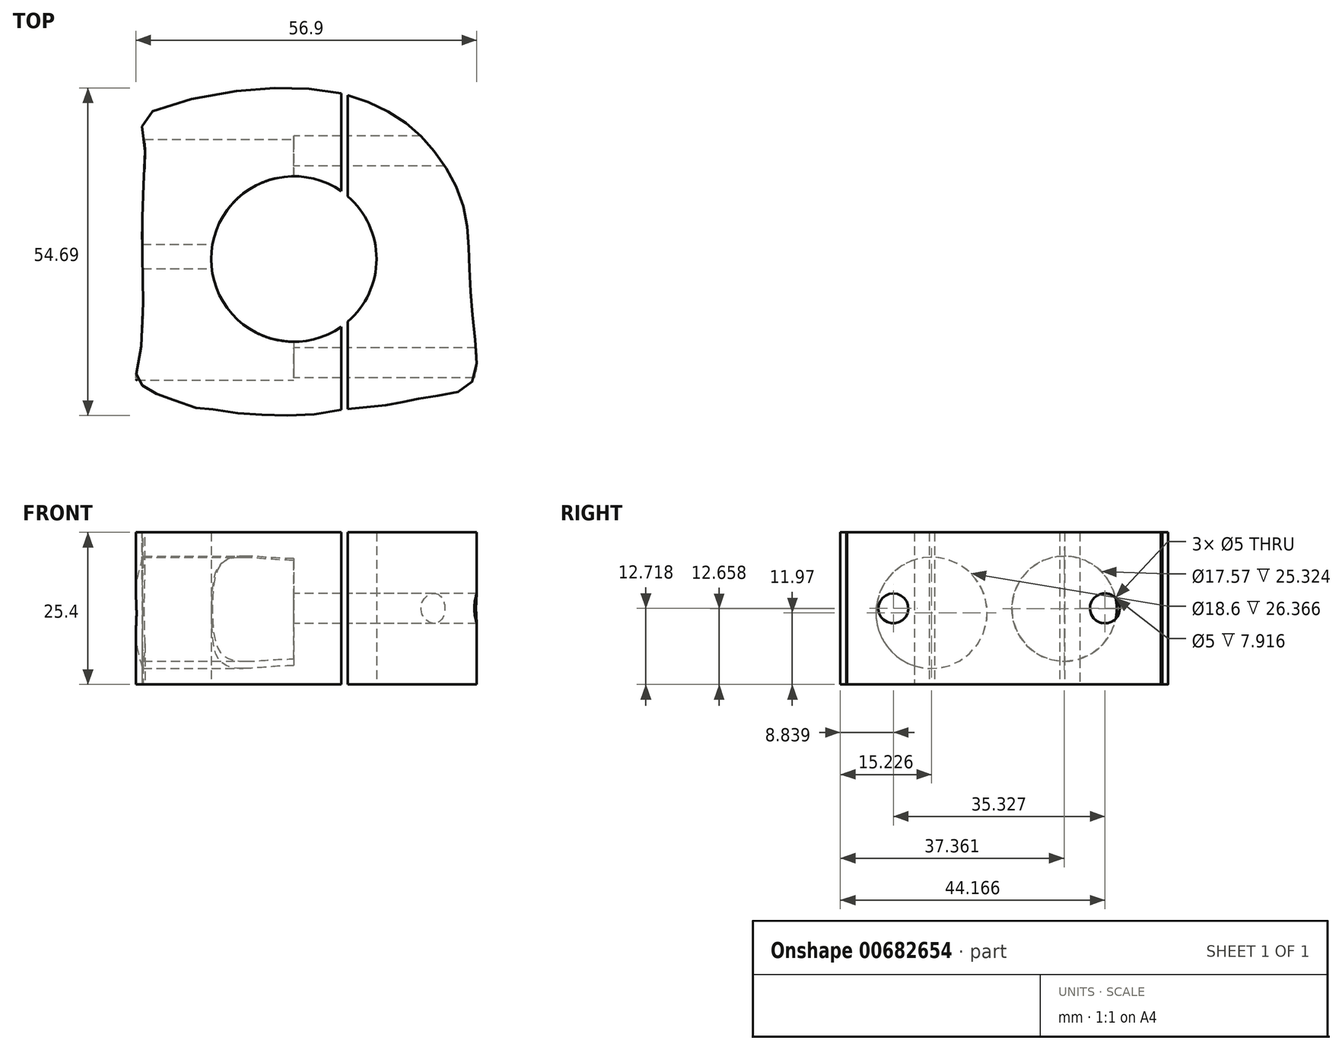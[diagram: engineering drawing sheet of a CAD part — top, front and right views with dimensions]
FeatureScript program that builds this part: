
annotation { "Feature Type Name" : "Feature", "Feature Type Description" : "" }
export const myFeature = defineFeature(function(context is Context, id is Id, definition is map)
    precondition{}
    {
        {
            var Q0;
            Q0=qCreatedBy(makeId("Top.planeOp"),FACE);
            var sketch = newSketch(context, id + "F0", { "sketchPlane" : qUnion([Q0])});
            skCircle(sketch, "E0", {"center": v(0, 0) * mm, "radius": 13.8 * mm});
            skFitSpline(sketch, "E1", {"points": [v(-26.3, -20.13) * mm, v(-25.31, -21.11) * mm, v(-23.34, -22.35) * mm, v(-20.62, -23.34) * mm, v(-16.42, -24.82) * mm, v(-13.95, -25.06) * mm, v(-8.77, -25.8) * mm, v(-3.83, -26.05) * mm, v(2.35, -26.05) * mm, v(8.77, -25.06) * mm, v(16.17, -24.32) * mm, v(22.1, -23.09) * mm, v(29.5, -20.87) * mm, v(30, -11.24) * mm, v(29.26, 0) * mm, v(28.28, 9.01) * mm, v(24.08, 17.16) * mm, v(18.15, 23.09) * mm, v(9.26, 27.29) * mm, v(0, 28.52) * mm, v(-12.96, 27.53) * mm, v(-25.06, 23.58) * mm, v(-25.06, 20.87) * mm, v(-25.06, 12.47) * mm, v(-25.31, 2.1) * mm, v(-25.56, -15.19) * mm, v(-26.3, -20.13) * mm]});
            skSolve(sketch);
        }
        {
            var Q0;
            Q0=makeQuery(id+"F0.imprint","IMPRINT",FACE,{"disambiguationData":[TD([[makeQuery(id+"F0.imprint","IMPRINT",EDGE,{"derivedFrom":sQuery(id+"F0.wireOp",EDGE,"E0")}),-1.0]])]});
            extrude(context, id + "F1", {"entities" : qUnion([Q0]), "depth" : 25.4 * mm, "offsetDistance" : 25.4 * mm});
        }
        {
            var Q0;
            Q0=qCreatedBy(makeId("Right.planeOp"),FACE);
            var sketch = newSketch(context, id + "F2", { "sketchPlane" : qUnion([Q0])});
            skCircle(sketch, "E2", {"center": v(11.21, 12.66) * mm, "radius": 8.78 * mm});
            skCircle(sketch, "E3", {"center": v(-10.92, 11.97) * mm, "radius": 9.3 * mm});
            skSolve(sketch);
        }
        {
            var Q0;
            Q0=makeQuery(id+"F2.imprint","IMPRINT",FACE,{"disambiguationData":[TD([[makeQuery(id+"F2.imprint","IMPRINT",EDGE,{"derivedFrom":sQuery(id+"F2.wireOp",EDGE,"E3")}),1.0]])]});
            var Q1;
            Q1=makeQuery(id+"F2.imprint","IMPRINT",FACE,{"disambiguationData":[TD([[makeQuery(id+"F2.imprint","IMPRINT",EDGE,{"derivedFrom":sQuery(id+"F2.wireOp",EDGE,"E2")}),1.0]])]});
            extrude(context, id + "F3", {"entities" : qUnion([Q0, Q1]), "operationType" : NewBodyOperationType.REMOVE, "endBound" : BoundingType.THROUGH_ALL, "oppositeDirection" : true, "depth" : 25.4 * mm, "offsetDistance" : 25.4 * mm});
        }
        {
            var Q0;
            Q0=qCreatedBy(makeId("Right.planeOp"),FACE);
            var sketch = newSketch(context, id + "F4", { "sketchPlane" : qUnion([Q0])});
            skPoint(sketch, "E4", {"position": v(-17.31, 12.72) * mm});
            skPoint(sketch, "E5", {"position": v(18.02, 12.72) * mm});
            skSolve(sketch);
        }
        {
            var Q0;
            Q0=sQuery(id+"F4.wireOp",VERTEX,"E4");
            var Q1;
            Q1=sQuery(id+"F4.wireOp",VERTEX,"E5");
            var Q2;
            Q2=makeQuery(id+"F1.opExtrude","SWEPT_BODY",BODY,{"disambiguationData":[OSD([sQuery(id+"F0.wireOp",EDGE,"E0"),sQuery(id+"F0.wireOp",EDGE,"E1")])]});
            hole(context, id + "F5", {"style" : HoleStyle.C_BORE, "endStyle" : HoleEndStyle.THROUGH, "oppositeDirection" : true, "standardTappedOrClearance" : lookupTablePath({ "standard" : "ISO", "size" : "5", "type" : "Drilled" }), "standardBlindInLast" : lookupTablePath({ "standard" : "ISO", "size" : "5", "type" : "Drilled" }), "holeDiameter" : 5 * mm, "cBoreDiameter" : 9.75 * mm, "cBoreDepth" : 0 * mm, "majorDiameter" : 5 * mm, "isTappedThrough" : true, "tappedDepth" : 12.7 * mm, "tapClearance" : 3, "locations" : qUnion([Q0, Q1]), "scope" : qUnion([Q2])});
        }
        {
            var Q0;
            Q0=qCreatedBy(makeId("Top.planeOp"),FACE);
            var sketch = newSketch(context, id + "F6", { "sketchPlane" : qUnion([Q0])});
            skLineSegment(sketch, "E6.bottom", {"start": v(7.92, -25.53) * mm, "end": v(9.01, -25.53) * mm});
            skLineSegment(sketch, "E6.top", {"start": v(7.92, 28.77) * mm, "end": v(9.01, 28.77) * mm});
            skLineSegment(sketch, "E6.left", {"start": v(7.92, -25.53) * mm, "end": v(7.92, 28.77) * mm});
            skLineSegment(sketch, "E6.right", {"start": v(9.01, -25.53) * mm, "end": v(9.01, 28.77) * mm});
            skSolve(sketch);
        }
        {
            var Q0;
            Q0 = qSketchRegion(id + "F6", true);
            extrude(context, id + "F7", {"entities" : qUnion([Q0]), "operationType" : NewBodyOperationType.REMOVE, "endBound" : BoundingType.THROUGH_ALL, "depth" : 635 * mm, "offsetDistance" : 25.4 * mm});
        }
    });
